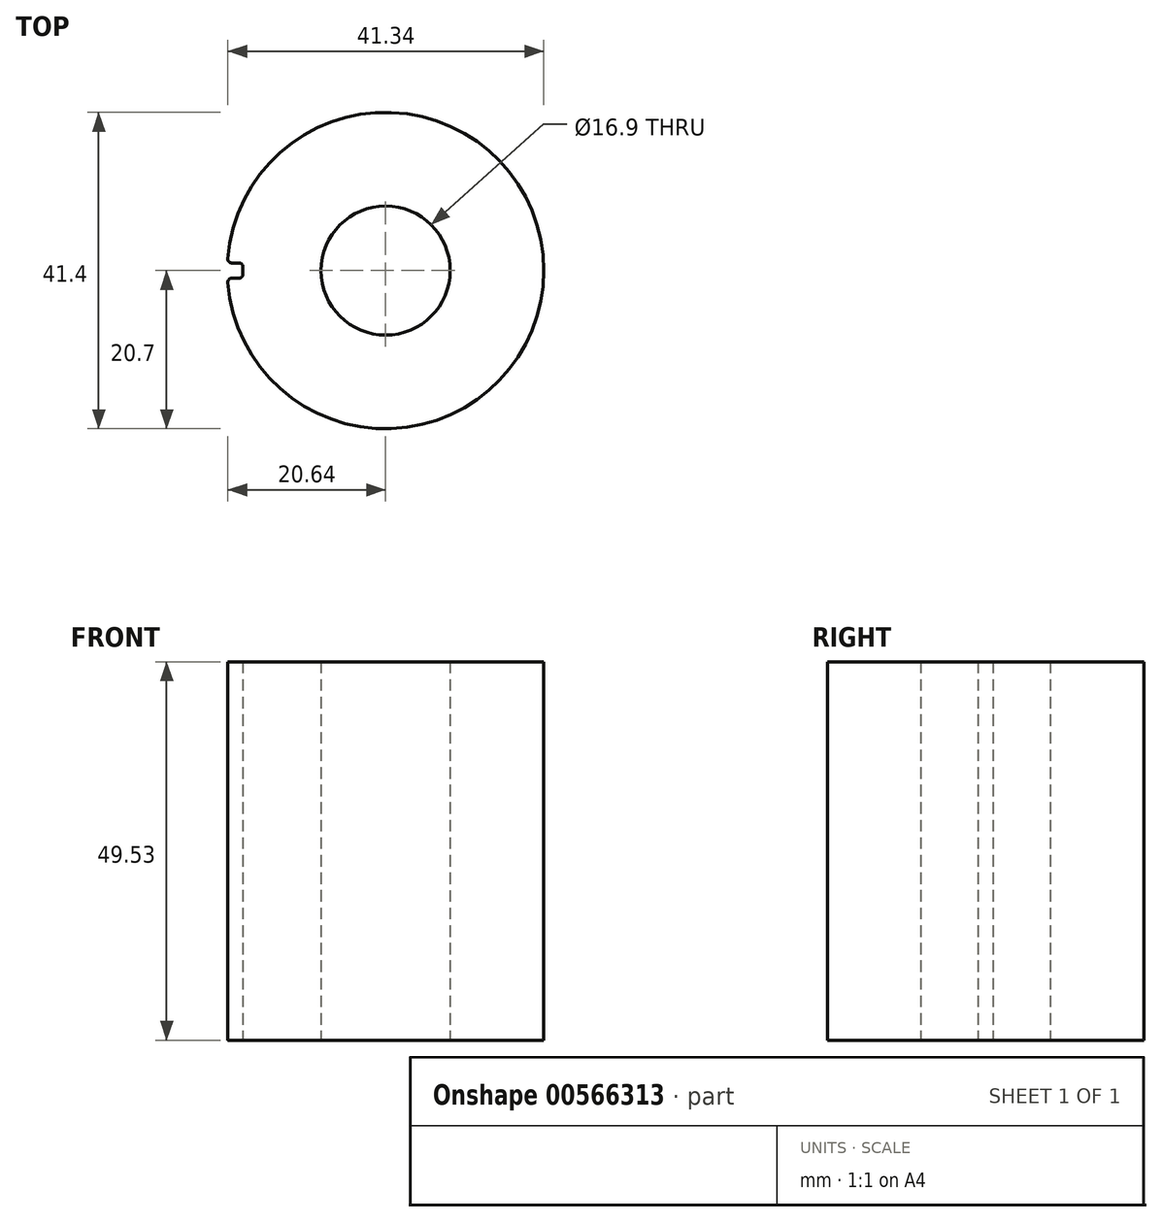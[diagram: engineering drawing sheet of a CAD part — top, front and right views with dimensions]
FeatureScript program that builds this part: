
annotation { "Feature Type Name" : "Feature", "Feature Type Description" : "" }
export const myFeature = defineFeature(function(context is Context, id is Id, definition is map)
    precondition{}
    {
        {
            var Q0;
            Q0=qCreatedBy(makeId("Top.planeOp"),FACE);
            var sketch = newSketch(context, id + "F0", { "sketchPlane" : qUnion([Q0])});
            skArc(sketch, "E0", {"start": v(-20.64, -1.54) * mm, "mid": v(20.7, 0) * mm, "end": v(-20.64, 1.54) * mm});
            skCircle(sketch, "E1", {"center": v(0, 0) * mm, "radius": 8.45 * mm});
            skLineSegment(sketch, "E2", {"start": v(-20.14, 1) * mm, "end": v(-19.18, 1) * mm});
            skLineSegment(sketch, "E3", {"start": v(-18.68, 0.5) * mm, "end": v(-18.68, -0.5) * mm});
            skLineSegment(sketch, "E4", {"start": v(-19.18, -1) * mm, "end": v(-20.14, -1) * mm});
            skPoint(sketch, "E5.visualSharp", {"position": v(-20.68, 1) * mm});
            skArc(sketch, "E5.filletArc", {"start": v(-20.64, 1.54) * mm, "mid": v(-20.51, 1.16) * mm, "end": v(-20.14, 1) * mm});
            skPoint(sketch, "E6.visualSharp", {"position": v(-20.68, -1) * mm});
            skArc(sketch, "E6.filletArc", {"start": v(-20.14, -1) * mm, "mid": v(-20.51, -1.16) * mm, "end": v(-20.64, -1.54) * mm});
            skPoint(sketch, "E7", {"position": v(-18.68, 0) * mm});
            skPoint(sketch, "E8.visualSharp", {"position": v(-18.68, 1) * mm});
            skArc(sketch, "E8.filletArc", {"start": v(-18.68, 0.5) * mm, "mid": v(-18.82, 0.85) * mm, "end": v(-19.18, 1) * mm});
            skPoint(sketch, "E9.visualSharp", {"position": v(-18.68, -1) * mm});
            skArc(sketch, "E9.filletArc", {"start": v(-19.18, -1) * mm, "mid": v(-18.82, -0.85) * mm, "end": v(-18.68, -0.5) * mm});
            skSolve(sketch);
        }
        {
            var Q0;
            Q0=makeQuery(id+"F0.imprint","IMPRINT",FACE,{"disambiguationData":[TD([[makeQuery(id+"F0.imprint","IMPRINT",EDGE,{"derivedFrom":sQuery(id+"F0.wireOp",EDGE,"E0")}),1.0]])]});
            extrude(context, id + "F1", {"entities" : qUnion([Q0]), "depth" : 247.65 * mm / 5, "offsetDistance" : 25 * mm});
        }
    });
